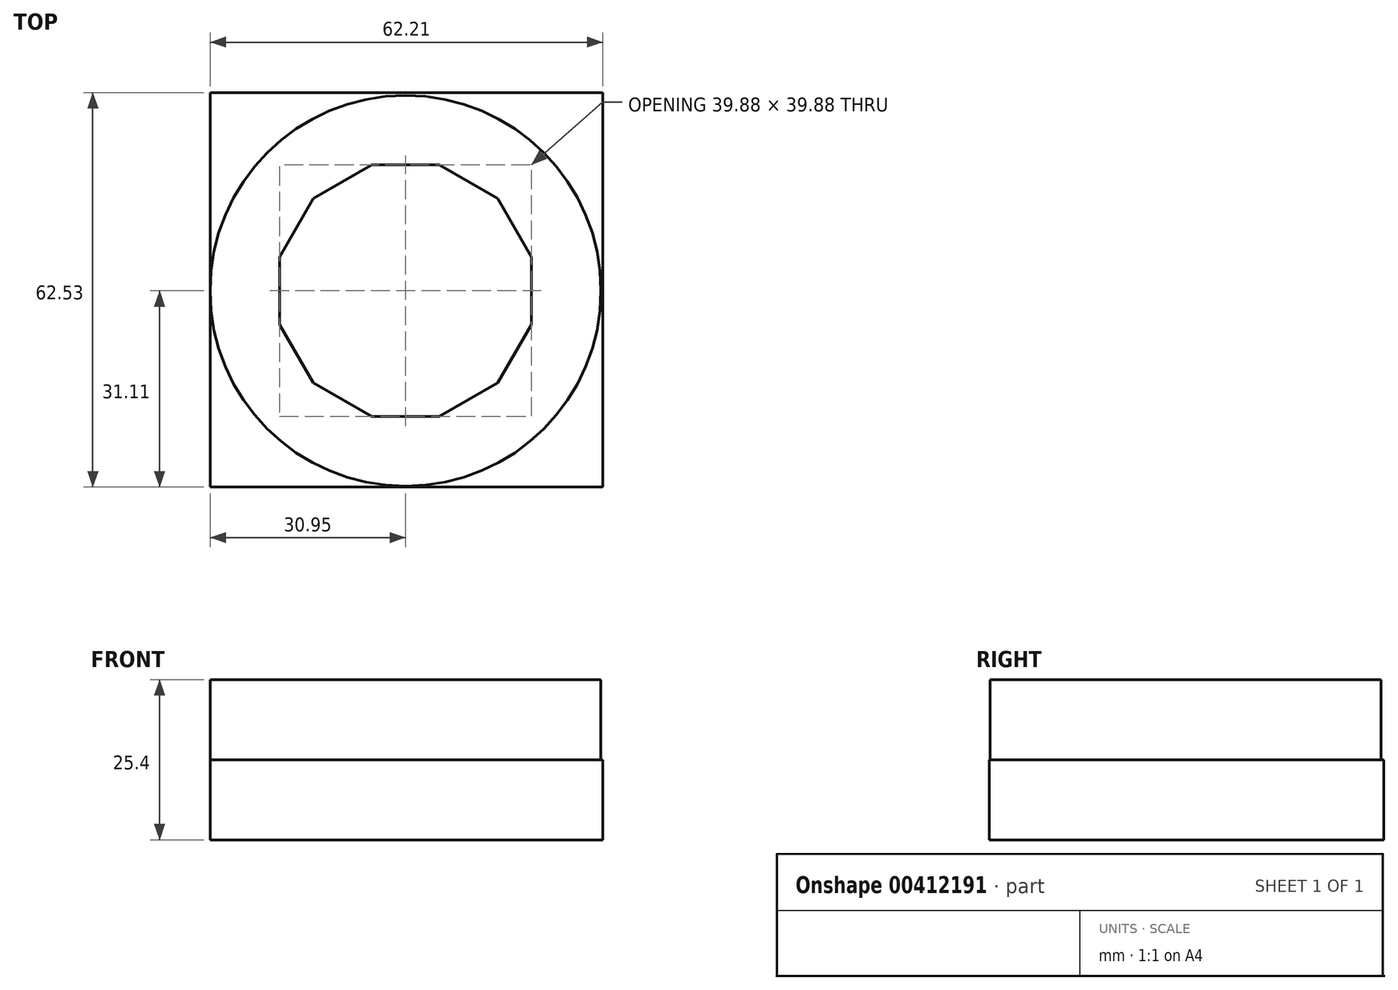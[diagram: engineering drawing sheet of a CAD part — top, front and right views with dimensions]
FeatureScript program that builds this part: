
annotation { "Feature Type Name" : "Feature", "Feature Type Description" : "" }
export const myFeature = defineFeature(function(context is Context, id is Id, definition is map)
    precondition{}
    {
        {
            var Q0;
            Q0=qCreatedBy(makeId("Top.planeOp"),FACE);
            var sketch = newSketch(context, id + "F0", { "sketchPlane" : qUnion([Q0])});
            skLineSegment(sketch, "E0.bottom", {"start": v(-30.95, 31.42) * mm, "end": v(31.26, 31.42) * mm});
            skLineSegment(sketch, "E0.top", {"start": v(-30.95, -31.1) * mm, "end": v(31.26, -31.1) * mm});
            skLineSegment(sketch, "E0.left", {"start": v(-30.95, 31.42) * mm, "end": v(-30.95, -31.1) * mm});
            skLineSegment(sketch, "E0.right", {"start": v(31.26, 31.42) * mm, "end": v(31.26, -31.1) * mm});
            skCircle(sketch, "E1", {"center": v(0, 0) * mm, "radius": 30.95 * mm});
            skCircle(sketch, "E2", {"center": v(0, 0) * mm, "radius": 7.52 * mm});
            skCircle(sketch, "E3.cCircle", {"center": v(0, 0) * mm, "radius": 19.94 * mm, "construction": true});
            skLineSegment(sketch, "E3.0", {"start": v(-19.94, -5.34) * mm, "end": v(-19.94, 5.34) * mm});
            skLineSegment(sketch, "E3.1", {"start": v(-19.94, 5.34) * mm, "end": v(-14.6, 14.6) * mm});
            skLineSegment(sketch, "E3.2", {"start": v(-14.6, 14.6) * mm, "end": v(-5.34, 19.94) * mm});
            skLineSegment(sketch, "E3.3", {"start": v(-5.34, 19.94) * mm, "end": v(5.34, 19.94) * mm});
            skLineSegment(sketch, "E3.4", {"start": v(5.34, 19.94) * mm, "end": v(14.6, 14.6) * mm});
            skLineSegment(sketch, "E3.5", {"start": v(14.6, 14.6) * mm, "end": v(19.94, 5.34) * mm});
            skLineSegment(sketch, "E3.6", {"start": v(19.94, 5.34) * mm, "end": v(19.94, -5.34) * mm});
            skLineSegment(sketch, "E3.7", {"start": v(19.94, -5.34) * mm, "end": v(14.6, -14.6) * mm});
            skLineSegment(sketch, "E3.8", {"start": v(14.6, -14.6) * mm, "end": v(5.34, -19.94) * mm});
            skLineSegment(sketch, "E3.9", {"start": v(5.34, -19.94) * mm, "end": v(-5.34, -19.94) * mm});
            skLineSegment(sketch, "E3.10", {"start": v(-5.34, -19.94) * mm, "end": v(-14.6, -14.6) * mm});
            skLineSegment(sketch, "E3.11", {"start": v(-14.6, -14.6) * mm, "end": v(-19.94, -5.34) * mm});
            skPoint(sketch, "E3.0.midPoint", {"position": v(-19.94, 0) * mm});
            skSolve(sketch);
        }
        {
            var Q0;
            Q0=makeQuery(id+"F0.imprint","IMPRINT",FACE,{"disambiguationData":[TD([[makeQuery(id+"F0.imprint","IMPRINT",EDGE,{"derivedFrom":sQuery(id+"F0.wireOp",EDGE,"E1")}),1.0]])]});
            extrude(context, id + "F1", {"entities" : qUnion([Q0]), "depth" : 25.4 * mm});
        }
        {
            var Q0;
            Q0 = qSketchRegion(id + "F0", true);
            extrude(context, id + "F2", {"entities" : qUnion([Q0]), "operationType" : NewBodyOperationType.ADD, "depth" : 12.7 * mm});
        }
    });
